# Revit family: KB d=600_Precast-Console Beam_Spæncom
name_source: partatom
category: Structural Framing
revit_build: Autodesk Revit 2014 (Build: 20130308_1515(x64)
units: mm (PartAtom-declared; Revit-internal decimal feet)

## types (9) — shared parameters
Base width = 500 mm  [stored 1.64042 ft]
Height console = 600 mm  [stored 1.9685 ft]
Manufacturer = Spæncom
Width (bjælkekroppen) = 350 mm  [stored 1.14829 ft]
Width console = 150 mm

## per-type parameters (varying)
| type | Height (bjælkekroppen) | Height element | Model |
| KB78/18 | 180 mm  [stored 0.590551 ft] | 780 mm  [stored 2.55906 ft] | KB 78/18 |
| KB82/22 | 220 mm  [stored 0.721785 ft] | 820 mm  [stored 2.69029 ft] | KB 82/22 |
| KB87/27 | 270 mm  [stored 0.885827 ft] | 870 mm  [stored 2.85433 ft] | KB 87/27 |
| KB92/32 | 320 mm  [stored 1.04987 ft] | 920 mm  [stored 3.01837 ft] | KB 92/32 |
| KB97/37 | 370 mm  [stored 1.21391 ft] | 970 mm  [stored 3.18241 ft] | KB 97/37 |
| KB90/30 | 300 mm | 900 mm  [stored 2.95276 ft] | KB 90/30 |
| KB100/40 | 400 mm  [stored 1.31234 ft] | 1000 mm  [stored 3.28084 ft] | KB 100/40 |
| KB110/50 | 500 mm  [stored 1.64042 ft] | 1100 mm | KB 110/50 |
| KB120/60 | 600 mm  [stored 1.9685 ft] | 1200 mm | KB 120/60 |

note: [stored X ft] marks values corroborated as IEEE doubles in the binary element streams (Revit-internal decimal feet)

## geometry (parser evidence)
native form markers: Sweep x6
no freeform markers — native parametric forms only
